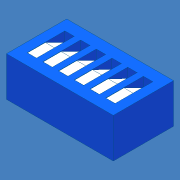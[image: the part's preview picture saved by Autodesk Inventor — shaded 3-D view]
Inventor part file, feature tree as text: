
AUTODESK INVENTOR PART (.ipt)
format: ipt  version: 2011 (Build 150239000, 239)  size: 154,624 bytes
history: native  units: mm (DEFAULTED — no unit token found)
features: extrude x4, sketch x4, pattern_linear x2
ambient origin geometry x8: Origin, YZ Plane, XZ Plane, XY Plane, X Axis, Y Axis, Z Axis, Center Point
bodies: Solid1 (feature_tree)
feature tree (10):
  extrude  "Extrusion1"  Depth=17.272mm
  extrude  "Extrusion2"  Depth=1.524mm
  extrude  "Extrusion6"  Depth=1.524mm
  extrude  "Extrusion7"  Depth=0.0254mm
  pattern_linear  "Rectangular Pattern5"  Spacing1=2.5146mm  [1 undecoded]
  pattern_linear  "Rectangular Pattern6"  Spacing1=3.175mm  [1 undecoded]
  sketch  "Sketch1"  dims[d0=9.7409mm d1=17.272mm]
  sketch  "Sketch2"  dims[d2=6.3881mm d3=0.0mm d4=1.524mm]
  sketch  "Sketch6"  dims[d5=6.096mm d7=1.524mm]
  sketch  "Sketch7"  dims[d8=2.54mm d9=0.0mm d38=0.0254mm d39=2.5146mm d40=0.0mm d41=3.175mm d42=1.5875mm d43=2.54mm d44=0.0mm d45=60.0mm d47=2.54mm d48=60.0mm d50=2.54mm]
note: 2 required parameter values undecoded (feature->parameter linkage not recoverable at this tier; creation-order binding heuristic only, values carry confidence <= 0.55)
